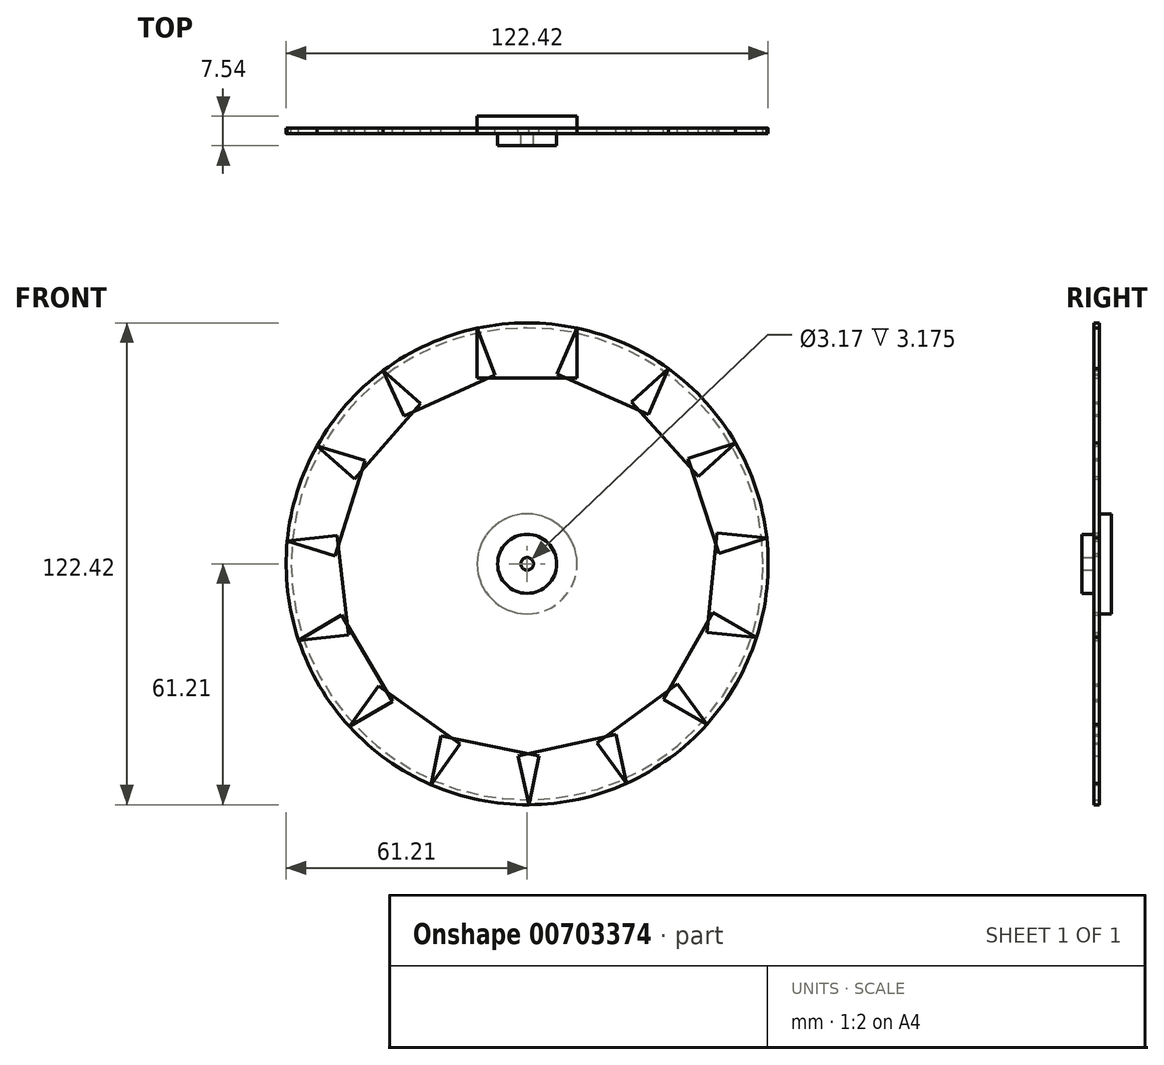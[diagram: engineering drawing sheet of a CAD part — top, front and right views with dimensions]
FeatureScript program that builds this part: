
annotation { "Feature Type Name" : "Feature", "Feature Type Description" : "" }
export const myFeature = defineFeature(function(context is Context, id is Id, definition is map)
    precondition{}
    {
        {
            var Q0;
            Q0=qCreatedBy(makeId("Front.planeOp"),FACE);
            var sketch = newSketch(context, id + "F0", { "sketchPlane" : qUnion([Q0])});
            skCircle(sketch, "E0", {"center": v(0, 0) * mm, "radius": 59.94 * mm});
            skCircle(sketch, "E1", {"center": v(0, 0) * mm, "radius": 61.21 * mm});
            skLineSegment(sketch, "E2.top", {"start": v(-12.7, 47.18) * mm, "end": v(12.7, 47.18) * mm});
            skLineSegment(sketch, "E2.left", {"start": v(-12.7, 59.88) * mm, "end": v(-12.7, 47.18) * mm});
            skLineSegment(sketch, "E2.right", {"start": v(12.7, 59.88) * mm, "end": v(12.7, 47.18) * mm});
            skArc(sketch, "E3", {"start": v(-12.7, 59.88) * mm, "mid": v(0, 61.21) * mm, "end": v(12.7, 59.88) * mm});
            skLineSegment(sketch, "E4.top", {"start": v(7.54, 48.28) * mm, "end": v(30.76, 37.97) * mm});
            skLineSegment(sketch, "E4.left", {"start": v(12.7, 59.88) * mm, "end": v(7.54, 48.28) * mm});
            skLineSegment(sketch, "E4.right", {"start": v(35.91, 49.57) * mm, "end": v(30.76, 37.97) * mm});
            skArc(sketch, "E5", {"start": v(12.7, 59.88) * mm, "mid": v(24.85, 55.94) * mm, "end": v(35.91, 49.57) * mm});
            skLineSegment(sketch, "E6.top", {"start": v(26.5, 41.06) * mm, "end": v(43.52, 22.21) * mm});
            skLineSegment(sketch, "E6.left", {"start": v(35.91, 49.57) * mm, "end": v(26.5, 41.06) * mm});
            skLineSegment(sketch, "E6.right", {"start": v(52.94, 30.73) * mm, "end": v(43.52, 22.21) * mm});
            skArc(sketch, "E7", {"start": v(35.91, 49.57) * mm, "mid": v(45.42, 41.04) * mm, "end": v(52.94, 30.73) * mm});
            skLineSegment(sketch, "E8.top", {"start": v(40.88, 26.77) * mm, "end": v(48.8, 2.63) * mm});
            skLineSegment(sketch, "E8.left", {"start": v(52.94, 30.73) * mm, "end": v(40.88, 26.77) * mm});
            skLineSegment(sketch, "E8.right", {"start": v(60.86, 6.6) * mm, "end": v(48.8, 2.63) * mm});
            skArc(sketch, "E9", {"start": v(52.94, 30.73) * mm, "mid": v(58.17, 19.07) * mm, "end": v(60.86, 6.6) * mm});
            skLineSegment(sketch, "E10.top", {"start": v(48.22, 7.87) * mm, "end": v(45.66, -17.4) * mm});
            skLineSegment(sketch, "E10.left", {"start": v(60.86, 6.6) * mm, "end": v(48.22, 7.87) * mm});
            skLineSegment(sketch, "E10.right", {"start": v(58.3, -18.68) * mm, "end": v(45.66, -17.4) * mm});
            skArc(sketch, "E11", {"start": v(60.86, 6.6) * mm, "mid": v(60.9, -6.18) * mm, "end": v(58.3, -18.68) * mm});
            skLineSegment(sketch, "E12.top", {"start": v(47.27, -12.38) * mm, "end": v(34.67, -34.43) * mm});
            skLineSegment(sketch, "E12.left", {"start": v(58.3, -18.68) * mm, "end": v(47.27, -12.38) * mm});
            skLineSegment(sketch, "E12.right", {"start": v(45.7, -40.73) * mm, "end": v(34.67, -34.43) * mm});
            skArc(sketch, "E13", {"start": v(58.3, -18.68) * mm, "mid": v(53.15, -30.37) * mm, "end": v(45.7, -40.73) * mm});
            skLineSegment(sketch, "E14.top", {"start": v(38.17, -30.5) * mm, "end": v(17.7, -45.54) * mm});
            skLineSegment(sketch, "E14.left", {"start": v(45.7, -40.73) * mm, "end": v(38.17, -30.5) * mm});
            skLineSegment(sketch, "E14.right", {"start": v(25.23, -55.77) * mm, "end": v(17.7, -45.54) * mm});
            skArc(sketch, "E15", {"start": v(45.7, -40.73) * mm, "mid": v(36.25, -49.33) * mm, "end": v(25.23, -55.77) * mm});
            skLineSegment(sketch, "E16.top", {"start": v(22.5, -43.37) * mm, "end": v(-2.3, -48.8) * mm});
            skLineSegment(sketch, "E16.left", {"start": v(25.23, -55.77) * mm, "end": v(22.5, -43.37) * mm});
            skLineSegment(sketch, "E16.right", {"start": v(0.42, -61.21) * mm, "end": v(-2.3, -48.8) * mm});
            skArc(sketch, "E17", {"start": v(25.23, -55.77) * mm, "mid": v(13.1, -59.8) * mm, "end": v(0.42, -61.21) * mm});
            skLineSegment(sketch, "E18.top", {"start": v(2.97, -48.77) * mm, "end": v(-21.92, -43.67) * mm});
            skLineSegment(sketch, "E18.left", {"start": v(0.42, -61.21) * mm, "end": v(2.97, -48.77) * mm});
            skLineSegment(sketch, "E18.right", {"start": v(-24.47, -56.11) * mm, "end": v(-21.92, -43.67) * mm});
            skArc(sketch, "E19", {"start": v(0.42, -61.21) * mm, "mid": v(-12.3, -59.97) * mm, "end": v(-24.47, -56.11) * mm});
            skLineSegment(sketch, "E20.top", {"start": v(-17.09, -45.78) * mm, "end": v(-37.76, -31.01) * mm});
            skLineSegment(sketch, "E20.left", {"start": v(-24.47, -56.11) * mm, "end": v(-17.09, -45.78) * mm});
            skLineSegment(sketch, "E20.right", {"start": v(-45.14, -41.35) * mm, "end": v(-37.76, -31.01) * mm});
            skArc(sketch, "E21", {"start": v(-24.47, -56.11) * mm, "mid": v(-35.58, -49.81) * mm, "end": v(-45.14, -41.35) * mm});
            skLineSegment(sketch, "E22.top", {"start": v(-34.2, -34.9) * mm, "end": v(-47.1, -13.02) * mm});
            skLineSegment(sketch, "E22.left", {"start": v(-45.14, -41.35) * mm, "end": v(-34.2, -34.9) * mm});
            skLineSegment(sketch, "E22.right", {"start": v(-58.04, -19.47) * mm, "end": v(-47.1, -13.02) * mm});
            skArc(sketch, "E23", {"start": v(-45.14, -41.35) * mm, "mid": v(-52.73, -31.09) * mm, "end": v(-58.04, -19.47) * mm});
            skLineSegment(sketch, "E24.top", {"start": v(-45.42, -18.02) * mm, "end": v(-48.33, 7.22) * mm});
            skLineSegment(sketch, "E24.left", {"start": v(-58.04, -19.47) * mm, "end": v(-45.42, -18.02) * mm});
            skLineSegment(sketch, "E24.right", {"start": v(-60.94, 5.76) * mm, "end": v(-48.33, 7.22) * mm});
            skArc(sketch, "E25", {"start": v(-58.04, -19.47) * mm, "mid": v(-60.81, -7) * mm, "end": v(-60.94, 5.76) * mm});
            skLineSegment(sketch, "E26.top", {"start": v(-48.82, 1.97) * mm, "end": v(-41.24, 26.21) * mm});
            skLineSegment(sketch, "E26.left", {"start": v(-60.94, 5.76) * mm, "end": v(-48.82, 1.97) * mm});
            skLineSegment(sketch, "E26.right", {"start": v(-53.36, 30) * mm, "end": v(-41.24, 26.21) * mm});
            skArc(sketch, "E27", {"start": v(-60.94, 5.76) * mm, "mid": v(-58.42, 18.28) * mm, "end": v(-53.36, 30) * mm});
            skLineSegment(sketch, "E28.top", {"start": v(-43.82, 21.62) * mm, "end": v(-27.05, 40.7) * mm});
            skLineSegment(sketch, "E28.left", {"start": v(-53.36, 30) * mm, "end": v(-43.82, 21.62) * mm});
            skLineSegment(sketch, "E28.right", {"start": v(-36.58, 49.08) * mm, "end": v(-27.05, 40.7) * mm});
            skArc(sketch, "E29", {"start": v(-53.36, 30) * mm, "mid": v(-45.97, 40.42) * mm, "end": v(-36.58, 49.08) * mm});
            skLineSegment(sketch, "E30.top", {"start": v(-31.34, 37.51) * mm, "end": v(-8.2, 48) * mm});
            skLineSegment(sketch, "E30.left", {"start": v(-36.58, 49.08) * mm, "end": v(-31.34, 37.51) * mm});
            skArc(sketch, "E31", {"start": v(-36.58, 49.08) * mm, "mid": v(49.94, -35.4) * mm, "end": v(-58.42, 18.28) * mm});
            skArc(sketch, "E32", {"start": v(-58.42, 18.28) * mm, "mid": v(-6.8, 60.84) * mm, "end": v(52.94, 30.73) * mm});
            skCircle(sketch, "E33", {"center": v(0, 0) * mm, "radius": 7.5 * mm});
            skArc(sketch, "E34", {"start": v(-58.42, 18.28) * mm, "mid": v(-41.2, 45.28) * mm, "end": v(-12.7, 59.88) * mm});
            skLineSegment(sketch, "E35", {"start": v(-12.7, 59.88) * mm, "end": v(-8.2, 48) * mm});
            skPoint(sketch, "E36", {"position": v(-35.43, 31.16) * mm});
            skPoint(sketch, "E37", {"position": v(-19.77, 42.76) * mm});
            skPoint(sketch, "E38", {"position": v(0, 47.18) * mm});
            skPoint(sketch, "E39", {"position": v(19.15, 43.12) * mm});
            skPoint(sketch, "E40", {"position": v(35, 31.63) * mm});
            skPoint(sketch, "E41", {"position": v(44.83, 14.7) * mm});
            skPoint(sketch, "E42", {"position": v(46.94, -4.76) * mm});
            skPoint(sketch, "E43", {"position": v(40.97, -23.4) * mm});
            skPoint(sketch, "E44", {"position": v(27.94, -38.02) * mm});
            skPoint(sketch, "E45", {"position": v(10.1, -46.09) * mm});
            skPoint(sketch, "E46", {"position": v(-9.48, -46.22) * mm});
            skPoint(sketch, "E47", {"position": v(-27.42, -38.4) * mm});
            skPoint(sketch, "E48", {"position": v(-40.65, -23.96) * mm});
            skPoint(sketch, "E49", {"position": v(-46.87, -5.4) * mm});
            skPoint(sketch, "E50", {"position": v(-45.03, 14.1) * mm});
            skSolve(sketch);
        }
        {
            var Q0;
            {var subQ7=sQuery(id+"F0.wireOp",EDGE,"E0");var subQ9=sQuery(id+"F0.wireOp",EDGE,"E6.left");var subQ10=makeQuery(id+"F0.imprint","INTERSECT",VERTEX,{"derivedFrom":[subQ7,subQ9]});Q0=makeQuery(id+"F0.imprint","IMPRINT",FACE,{"disambiguationData":[TD([[makeQuery(id+"F0.imprint","IMPRINT",EDGE,{"disambiguationData":[TD([[subQ10,-1.0]])],"derivedFrom":subQ7}),1.0]])]});}
            var Q1;
            {var subQ7=sQuery(id+"F0.wireOp",EDGE,"E0");var subQ9=sQuery(id+"F0.wireOp",EDGE,"E20.left");var subQ10=makeQuery(id+"F0.imprint","INTERSECT",VERTEX,{"derivedFrom":[subQ7,subQ9]});Q1=makeQuery(id+"F0.imprint","IMPRINT",FACE,{"disambiguationData":[TD([[makeQuery(id+"F0.imprint","IMPRINT",EDGE,{"disambiguationData":[TD([[subQ10,-1.0]])],"derivedFrom":subQ7}),1.0]])]});}
            var Q2;
            {var subQ0=sQuery(id+"F0.wireOp",EDGE,"E20.right");var subQ3=sQuery(id+"F0.wireOp",EDGE,"E0");var subQ4=makeQuery(id+"F0.imprint","INTERSECT",VERTEX,{"derivedFrom":[subQ3,subQ0]});Q2=makeQuery(id+"F0.imprint","IMPRINT",FACE,{"disambiguationData":[TD([[makeQuery(id+"F0.imprint","IMPRINT",EDGE,{"disambiguationData":[TD([[subQ4,-1.0]])],"derivedFrom":subQ3}),1.0]])]});}
            var Q3;
            {var subQ0=sQuery(id+"F0.wireOp",EDGE,"E14.right");var subQ3=sQuery(id+"F0.wireOp",EDGE,"E0");var subQ4=makeQuery(id+"F0.imprint","INTERSECT",VERTEX,{"derivedFrom":[subQ3,subQ0]});Q3=makeQuery(id+"F0.imprint","IMPRINT",FACE,{"disambiguationData":[TD([[makeQuery(id+"F0.imprint","IMPRINT",EDGE,{"disambiguationData":[TD([[subQ4,-1.0]])],"derivedFrom":subQ3}),1.0]])]});}
            var Q4;
            {var subQ0=sQuery(id+"F0.wireOp",EDGE,"E10.right");var subQ3=sQuery(id+"F0.wireOp",EDGE,"E0");var subQ4=makeQuery(id+"F0.imprint","INTERSECT",VERTEX,{"derivedFrom":[subQ3,subQ0]});Q4=makeQuery(id+"F0.imprint","IMPRINT",FACE,{"disambiguationData":[TD([[makeQuery(id+"F0.imprint","IMPRINT",EDGE,{"disambiguationData":[TD([[subQ4,-1.0]])],"derivedFrom":subQ3}),1.0]])]});}
            var Q5;
            {var subQ7=sQuery(id+"F0.wireOp",EDGE,"E0");var subQ9=sQuery(id+"F0.wireOp",EDGE,"E26.left");var subQ10=makeQuery(id+"F0.imprint","INTERSECT",VERTEX,{"derivedFrom":[subQ7,subQ9]});Q5=makeQuery(id+"F0.imprint","IMPRINT",FACE,{"disambiguationData":[TD([[makeQuery(id+"F0.imprint","IMPRINT",EDGE,{"disambiguationData":[TD([[subQ10,-1.0]])],"derivedFrom":subQ7}),1.0]])]});}
            var Q6;
            {var subQ5=sQuery(id+"F0.wireOp",EDGE,"E12.right");var subQ7=sQuery(id+"F0.wireOp",EDGE,"E0");var subQ8=makeQuery(id+"F0.imprint","INTERSECT",VERTEX,{"derivedFrom":[subQ7,subQ5]});Q6=makeQuery(id+"F0.imprint","IMPRINT",FACE,{"disambiguationData":[TD([[makeQuery(id+"F0.imprint","IMPRINT",EDGE,{"disambiguationData":[TD([[subQ8,-1.0]])],"derivedFrom":subQ7}),1.0]])]});}
            var Q7;
            {var subQ0=sQuery(id+"F0.wireOp",EDGE,"E26.right");var subQ3=sQuery(id+"F0.wireOp",EDGE,"E0");var subQ4=makeQuery(id+"F0.imprint","INTERSECT",VERTEX,{"derivedFrom":[subQ3,subQ0]});Q7=makeQuery(id+"F0.imprint","IMPRINT",FACE,{"disambiguationData":[TD([[makeQuery(id+"F0.imprint","IMPRINT",EDGE,{"disambiguationData":[TD([[subQ4,-1.0]])],"derivedFrom":subQ3}),1.0]])]});}
            var Q8;
            {var subQ0=sQuery(id+"F0.wireOp",EDGE,"E24.right");var subQ3=sQuery(id+"F0.wireOp",EDGE,"E0");var subQ4=makeQuery(id+"F0.imprint","INTERSECT",VERTEX,{"derivedFrom":[subQ3,subQ0]});Q8=makeQuery(id+"F0.imprint","IMPRINT",FACE,{"disambiguationData":[TD([[makeQuery(id+"F0.imprint","IMPRINT",EDGE,{"disambiguationData":[TD([[subQ4,-1.0]])],"derivedFrom":subQ3}),1.0]])]});}
            var Q9;
            {var subQ5=sQuery(id+"F0.wireOp",EDGE,"E22.right");var subQ7=sQuery(id+"F0.wireOp",EDGE,"E0");var subQ8=makeQuery(id+"F0.imprint","INTERSECT",VERTEX,{"derivedFrom":[subQ7,subQ5]});Q9=makeQuery(id+"F0.imprint","IMPRINT",FACE,{"disambiguationData":[TD([[makeQuery(id+"F0.imprint","IMPRINT",EDGE,{"disambiguationData":[TD([[subQ8,-1.0]])],"derivedFrom":subQ7}),1.0]])]});}
            var Q10;
            {var subQ7=sQuery(id+"F0.wireOp",EDGE,"E0");var subQ9=sQuery(id+"F0.wireOp",EDGE,"E8.left");var subQ10=makeQuery(id+"F0.imprint","INTERSECT",VERTEX,{"derivedFrom":[subQ7,subQ9]});Q10=makeQuery(id+"F0.imprint","IMPRINT",FACE,{"disambiguationData":[TD([[makeQuery(id+"F0.imprint","IMPRINT",EDGE,{"disambiguationData":[TD([[subQ10,-1.0]])],"derivedFrom":subQ7}),1.0]])]});}
            var Q11;
            {var subQ0=sQuery(id+"F0.wireOp",EDGE,"E18.right");var subQ3=sQuery(id+"F0.wireOp",EDGE,"E0");var subQ4=makeQuery(id+"F0.imprint","INTERSECT",VERTEX,{"derivedFrom":[subQ3,subQ0]});Q11=makeQuery(id+"F0.imprint","IMPRINT",FACE,{"disambiguationData":[TD([[makeQuery(id+"F0.imprint","IMPRINT",EDGE,{"disambiguationData":[TD([[subQ4,-1.0]])],"derivedFrom":subQ3}),1.0]])]});}
            var Q12;
            {var subQ7=sQuery(id+"F0.wireOp",EDGE,"E0");var subQ9=sQuery(id+"F0.wireOp",EDGE,"E14.left");var subQ10=makeQuery(id+"F0.imprint","INTERSECT",VERTEX,{"derivedFrom":[subQ7,subQ9]});Q12=makeQuery(id+"F0.imprint","IMPRINT",FACE,{"disambiguationData":[TD([[makeQuery(id+"F0.imprint","IMPRINT",EDGE,{"disambiguationData":[TD([[subQ10,-1.0]])],"derivedFrom":subQ7}),1.0]])]});}
            var Q13;
            {var subQ5=sQuery(id+"F0.wireOp",EDGE,"E2.right");var subQ7=sQuery(id+"F0.wireOp",EDGE,"E0");var subQ8=makeQuery(id+"F0.imprint","INTERSECT",VERTEX,{"derivedFrom":[subQ7,subQ5]});Q13=makeQuery(id+"F0.imprint","IMPRINT",FACE,{"disambiguationData":[TD([[makeQuery(id+"F0.imprint","IMPRINT",EDGE,{"disambiguationData":[TD([[subQ8,-1.0]])],"derivedFrom":subQ7}),1.0]])]});}
            var Q14;
            {var subQ0=sQuery(id+"F0.wireOp",EDGE,"E4.right");var subQ3=sQuery(id+"F0.wireOp",EDGE,"E0");var subQ4=makeQuery(id+"F0.imprint","INTERSECT",VERTEX,{"derivedFrom":[subQ3,subQ0]});Q14=makeQuery(id+"F0.imprint","IMPRINT",FACE,{"disambiguationData":[TD([[makeQuery(id+"F0.imprint","IMPRINT",EDGE,{"disambiguationData":[TD([[subQ4,-1.0]])],"derivedFrom":subQ3}),1.0]])]});}
            var Q15;
            {var subQ0=sQuery(id+"F0.wireOp",EDGE,"E28.right");var subQ3=sQuery(id+"F0.wireOp",EDGE,"E0");var subQ4=makeQuery(id+"F0.imprint","INTERSECT",VERTEX,{"derivedFrom":[subQ3,subQ0]});Q15=makeQuery(id+"F0.imprint","IMPRINT",FACE,{"disambiguationData":[TD([[makeQuery(id+"F0.imprint","IMPRINT",EDGE,{"disambiguationData":[TD([[subQ4,-1.0]])],"derivedFrom":subQ3}),1.0]])]});}
            var Q16;
            {var subQ5=sQuery(id+"F0.wireOp",EDGE,"E24.left");var subQ6=sQuery(id+"F0.wireOp",EDGE,"E0");var subQ7=makeQuery(id+"F0.imprint","INTERSECT",VERTEX,{"derivedFrom":[subQ6,subQ5]});Q16=makeQuery(id+"F0.imprint","IMPRINT",FACE,{"disambiguationData":[TD([[makeQuery(id+"F0.imprint","IMPRINT",EDGE,{"disambiguationData":[TD([[subQ7,-1.0]])],"derivedFrom":subQ6}),1.0]])]});}
            var Q17;
            {var subQ7=sQuery(id+"F0.wireOp",EDGE,"E0");var subQ9=sQuery(id+"F0.wireOp",EDGE,"E28.left");var subQ10=makeQuery(id+"F0.imprint","INTERSECT",VERTEX,{"derivedFrom":[subQ7,subQ9]});Q17=makeQuery(id+"F0.imprint","IMPRINT",FACE,{"disambiguationData":[TD([[makeQuery(id+"F0.imprint","IMPRINT",EDGE,{"disambiguationData":[TD([[subQ10,-1.0]])],"derivedFrom":subQ7}),1.0]])]});}
            var Q18;
            {var subQ3=sQuery(id+"F0.wireOp",EDGE,"E0");var subQ5=sQuery(id+"F0.wireOp",EDGE,"E22.left");var subQ6=makeQuery(id+"F0.imprint","INTERSECT",VERTEX,{"derivedFrom":[subQ3,subQ5]});Q18=makeQuery(id+"F0.imprint","IMPRINT",FACE,{"disambiguationData":[TD([[makeQuery(id+"F0.imprint","IMPRINT",EDGE,{"disambiguationData":[TD([[subQ6,-1.0]])],"derivedFrom":subQ3}),1.0]])]});}
            var Q19;
            {var subQ0=sQuery(id+"F0.wireOp",EDGE,"E16.right");var subQ3=sQuery(id+"F0.wireOp",EDGE,"E0");var subQ4=makeQuery(id+"F0.imprint","INTERSECT",VERTEX,{"derivedFrom":[subQ3,subQ0]});Q19=makeQuery(id+"F0.imprint","IMPRINT",FACE,{"disambiguationData":[TD([[makeQuery(id+"F0.imprint","IMPRINT",EDGE,{"disambiguationData":[TD([[subQ4,-1.0]])],"derivedFrom":subQ3}),1.0]])]});}
            var Q20;
            {var subQ0=sQuery(id+"F0.wireOp",EDGE,"E8.right");var subQ3=sQuery(id+"F0.wireOp",EDGE,"E0");var subQ4=makeQuery(id+"F0.imprint","INTERSECT",VERTEX,{"derivedFrom":[subQ3,subQ0]});Q20=makeQuery(id+"F0.imprint","IMPRINT",FACE,{"disambiguationData":[TD([[makeQuery(id+"F0.imprint","IMPRINT",EDGE,{"disambiguationData":[TD([[subQ4,1.0]])],"derivedFrom":subQ3}),1.0]])]});}
            var Q21;
            Q21=makeQuery(id+"F0.imprint","IMPRINT",FACE,{"disambiguationData":[TD([[makeQuery(id+"F0.imprint","IMPRINT",EDGE,{"derivedFrom":sQuery(id+"F0.wireOp",EDGE,"E33")}),-1.0]])]});
            var Q22;
            {var subQ7=sQuery(id+"F0.wireOp",EDGE,"E0");var subQ9=sQuery(id+"F0.wireOp",EDGE,"E16.left");var subQ10=makeQuery(id+"F0.imprint","INTERSECT",VERTEX,{"derivedFrom":[subQ7,subQ9]});Q22=makeQuery(id+"F0.imprint","IMPRINT",FACE,{"disambiguationData":[TD([[makeQuery(id+"F0.imprint","IMPRINT",EDGE,{"disambiguationData":[TD([[subQ10,-1.0]])],"derivedFrom":subQ7}),1.0]])]});}
            var Q23;
            {var subQ5=sQuery(id+"F0.wireOp",EDGE,"E10.left");var subQ6=sQuery(id+"F0.wireOp",EDGE,"E0");var subQ7=makeQuery(id+"F0.imprint","INTERSECT",VERTEX,{"derivedFrom":[subQ6,subQ5]});Q23=makeQuery(id+"F0.imprint","IMPRINT",FACE,{"disambiguationData":[TD([[makeQuery(id+"F0.imprint","IMPRINT",EDGE,{"disambiguationData":[TD([[subQ7,-1.0]])],"derivedFrom":subQ6}),1.0]])]});}
            var Q24;
            {var subQ3=sQuery(id+"F0.wireOp",EDGE,"E0");var subQ5=sQuery(id+"F0.wireOp",EDGE,"E10.left");var subQ9=makeQuery(id+"F0.imprint","INTERSECT",VERTEX,{"derivedFrom":[subQ3,subQ5]});Q24=makeQuery(id+"F0.imprint","IMPRINT",FACE,{"disambiguationData":[TD([[makeQuery(id+"F0.imprint","IMPRINT",EDGE,{"disambiguationData":[TD([[subQ9,1.0]])],"derivedFrom":subQ3}),1.0]])]});}
            var Q25;
            {var subQ0=sQuery(id+"F0.wireOp",EDGE,"E6.right");var subQ3=sQuery(id+"F0.wireOp",EDGE,"E0");var subQ4=makeQuery(id+"F0.imprint","INTERSECT",VERTEX,{"derivedFrom":[subQ3,subQ0]});Q25=makeQuery(id+"F0.imprint","IMPRINT",FACE,{"disambiguationData":[TD([[makeQuery(id+"F0.imprint","IMPRINT",EDGE,{"disambiguationData":[TD([[subQ4,-1.0]])],"derivedFrom":subQ3}),1.0]])]});}
            var Q26;
            {var subQ3=sQuery(id+"F0.wireOp",EDGE,"E0");var subQ5=sQuery(id+"F0.wireOp",EDGE,"E35");var subQ9=makeQuery(id+"F0.imprint","INTERSECT",VERTEX,{"derivedFrom":[subQ3,subQ5]});Q26=makeQuery(id+"F0.imprint","IMPRINT",FACE,{"disambiguationData":[TD([[makeQuery(id+"F0.imprint","IMPRINT",EDGE,{"disambiguationData":[TD([[subQ9,-1.0]])],"derivedFrom":subQ3}),1.0]])]});}
            var Q27;
            {var subQ7=sQuery(id+"F0.wireOp",EDGE,"E18.left");var subQ8=sQuery(id+"F0.wireOp",EDGE,"E0");var subQ9=makeQuery(id+"F0.imprint","INTERSECT",VERTEX,{"derivedFrom":[subQ8,subQ7]});Q27=makeQuery(id+"F0.imprint","IMPRINT",FACE,{"disambiguationData":[TD([[makeQuery(id+"F0.imprint","IMPRINT",EDGE,{"disambiguationData":[TD([[subQ9,-1.0]])],"derivedFrom":subQ8}),1.0]])]});}
            var Q28;
            {var subQ7=sQuery(id+"F0.wireOp",EDGE,"E0");var subQ9=sQuery(id+"F0.wireOp",EDGE,"E30.left");var subQ10=makeQuery(id+"F0.imprint","INTERSECT",VERTEX,{"derivedFrom":[subQ7,subQ9]});Q28=makeQuery(id+"F0.imprint","IMPRINT",FACE,{"disambiguationData":[TD([[makeQuery(id+"F0.imprint","IMPRINT",EDGE,{"disambiguationData":[TD([[subQ10,-1.0]])],"derivedFrom":subQ7}),1.0]])]});}
            var Q29;
            {var subQ5=sQuery(id+"F0.wireOp",EDGE,"E2.left");var subQ9=sQuery(id+"F0.wireOp",EDGE,"E0");var subQ10=makeQuery(id+"F0.imprint","INTERSECT",VERTEX,{"derivedFrom":[subQ9,subQ5]});Q29=makeQuery(id+"F0.imprint","IMPRINT",FACE,{"disambiguationData":[TD([[makeQuery(id+"F0.imprint","IMPRINT",EDGE,{"disambiguationData":[TD([[subQ10,-1.0]])],"derivedFrom":subQ9}),1.0]])]});}
            var Q30;
            {var subQ0=sQuery(id+"F0.wireOp",EDGE,"E4.left");var subQ3=sQuery(id+"F0.wireOp",EDGE,"E0");var subQ4=makeQuery(id+"F0.imprint","INTERSECT",VERTEX,{"derivedFrom":[subQ3,subQ0]});Q30=makeQuery(id+"F0.imprint","IMPRINT",FACE,{"disambiguationData":[TD([[makeQuery(id+"F0.imprint","IMPRINT",EDGE,{"disambiguationData":[TD([[subQ4,-1.0]])],"derivedFrom":subQ3}),1.0]])]});}
            extrude(context, id + "F1", {"entities" : qUnion([Q0, Q1, Q2, Q3, Q4, Q5, Q6, Q7, Q8, Q9, Q10, Q11, Q12, Q13, Q14, Q15, Q16, Q17, Q18, Q19, Q20, Q21, Q22, Q23, Q24, Q25, Q26, Q27, Q28, Q29, Q30]), "depth" : 1.2 * mm, "offsetDistance" : 25.4 * mm, "symmetric" : true});
        }
        {
            var Q0;
            {var subQ7=sQuery(id+"F0.wireOp",EDGE,"E0");var subQ9=sQuery(id+"F0.wireOp",EDGE,"E8.left");var subQ10=makeQuery(id+"F0.imprint","INTERSECT",VERTEX,{"derivedFrom":[subQ7,subQ9]});Q0=makeQuery(id+"F0.imprint","IMPRINT",FACE,{"disambiguationData":[TD([[makeQuery(id+"F0.imprint","IMPRINT",EDGE,{"disambiguationData":[TD([[subQ10,-1.0]])],"derivedFrom":subQ7}),1.0]])]});}
            var Q1;
            {var subQ0=sQuery(id+"F0.wireOp",EDGE,"E6.right");var subQ3=sQuery(id+"F0.wireOp",EDGE,"E0");var subQ4=makeQuery(id+"F0.imprint","INTERSECT",VERTEX,{"derivedFrom":[subQ3,subQ0]});Q1=makeQuery(id+"F0.imprint","IMPRINT",FACE,{"disambiguationData":[TD([[makeQuery(id+"F0.imprint","IMPRINT",EDGE,{"disambiguationData":[TD([[subQ4,-1.0]])],"derivedFrom":subQ3}),1.0]])]});}
            var Q2;
            {var subQ0=sQuery(id+"F0.wireOp",EDGE,"E4.right");var subQ3=sQuery(id+"F0.wireOp",EDGE,"E0");var subQ4=makeQuery(id+"F0.imprint","INTERSECT",VERTEX,{"derivedFrom":[subQ3,subQ0]});Q2=makeQuery(id+"F0.imprint","IMPRINT",FACE,{"disambiguationData":[TD([[makeQuery(id+"F0.imprint","IMPRINT",EDGE,{"disambiguationData":[TD([[subQ4,-1.0]])],"derivedFrom":subQ3}),1.0]])]});}
            var Q3;
            {var subQ0=sQuery(id+"F0.wireOp",EDGE,"E8.left");var subQ1=sQuery(id+"F0.wireOp",EDGE,"E0");var subQ2=makeQuery(id+"F0.imprint","INTERSECT",VERTEX,{"derivedFrom":[subQ1,subQ0]});Q3=makeQuery(id+"F0.imprint","IMPRINT",FACE,{"disambiguationData":[TD([[makeQuery(id+"F0.imprint","IMPRINT",EDGE,{"disambiguationData":[TD([[subQ2,-1.0]])],"derivedFrom":subQ1}),-1.0]])]});}
            var Q4;
            {var subQ0=sQuery(id+"F0.wireOp",EDGE,"E6.right");var subQ1=sQuery(id+"F0.wireOp",EDGE,"E0");var subQ2=makeQuery(id+"F0.imprint","INTERSECT",VERTEX,{"derivedFrom":[subQ1,subQ0]});Q4=makeQuery(id+"F0.imprint","IMPRINT",FACE,{"disambiguationData":[TD([[makeQuery(id+"F0.imprint","IMPRINT",EDGE,{"disambiguationData":[TD([[subQ2,-1.0]])],"derivedFrom":subQ1}),-1.0]])]});}
            var Q5;
            {var subQ0=sQuery(id+"F0.wireOp",EDGE,"E4.right");var subQ1=sQuery(id+"F0.wireOp",EDGE,"E0");var subQ2=makeQuery(id+"F0.imprint","INTERSECT",VERTEX,{"derivedFrom":[subQ1,subQ0]});Q5=makeQuery(id+"F0.imprint","IMPRINT",FACE,{"disambiguationData":[TD([[makeQuery(id+"F0.imprint","IMPRINT",EDGE,{"disambiguationData":[TD([[subQ2,-1.0]])],"derivedFrom":subQ1}),-1.0]])]});}
            extrude(context, id + "F2", {"entities" : qUnion([Q0, Q1, Q2, Q3, Q4, Q5]), "depth" : 1.2 * mm + .18 * mm, "offsetDistance" : 25.4 * mm, "symmetric" : true});
        }
        {
            var Q0;
            {var subQ0=sQuery(id+"F0.wireOp",EDGE,"E6.right");var subQ3=sQuery(id+"F0.wireOp",EDGE,"E0");var subQ4=makeQuery(id+"F0.imprint","INTERSECT",VERTEX,{"derivedFrom":[subQ3,subQ0]});Q0=makeQuery(id+"F0.imprint","IMPRINT",FACE,{"disambiguationData":[TD([[makeQuery(id+"F0.imprint","IMPRINT",EDGE,{"disambiguationData":[TD([[subQ4,-1.0]])],"derivedFrom":subQ3}),1.0]])]});}
            var Q1;
            {var subQ3=sQuery(id+"F0.wireOp",EDGE,"E0");var subQ9=sQuery(id+"F0.wireOp",EDGE,"E10.left");var subQ10=makeQuery(id+"F0.imprint","INTERSECT",VERTEX,{"derivedFrom":[subQ3,subQ9]});Q1=makeQuery(id+"F0.imprint","IMPRINT",FACE,{"disambiguationData":[TD([[makeQuery(id+"F0.imprint","IMPRINT",EDGE,{"disambiguationData":[TD([[subQ10,-1.0]])],"derivedFrom":subQ3}),1.0]])]});}
            var Q2;
            {var subQ0=sQuery(id+"F0.wireOp",EDGE,"E10.left");var subQ1=sQuery(id+"F0.wireOp",EDGE,"E0");var subQ2=makeQuery(id+"F0.imprint","INTERSECT",VERTEX,{"derivedFrom":[subQ1,subQ0]});Q2=makeQuery(id+"F0.imprint","IMPRINT",FACE,{"disambiguationData":[TD([[makeQuery(id+"F0.imprint","IMPRINT",EDGE,{"disambiguationData":[TD([[subQ2,-1.0]])],"derivedFrom":subQ1}),-1.0]])]});}
            var Q3;
            {var subQ3=sQuery(id+"F0.wireOp",EDGE,"E0");var subQ5=sQuery(id+"F0.wireOp",EDGE,"E10.left");var subQ9=makeQuery(id+"F0.imprint","INTERSECT",VERTEX,{"derivedFrom":[subQ3,subQ5]});Q3=makeQuery(id+"F0.imprint","IMPRINT",FACE,{"disambiguationData":[TD([[makeQuery(id+"F0.imprint","IMPRINT",EDGE,{"disambiguationData":[TD([[subQ9,1.0]])],"derivedFrom":subQ3}),1.0]])]});}
            var Q4;
            {var subQ0=sQuery(id+"F0.wireOp",EDGE,"E10.left");var subQ1=sQuery(id+"F0.wireOp",EDGE,"E0");var subQ2=makeQuery(id+"F0.imprint","INTERSECT",VERTEX,{"derivedFrom":[subQ1,subQ0]});Q4=makeQuery(id+"F0.imprint","IMPRINT",FACE,{"disambiguationData":[TD([[makeQuery(id+"F0.imprint","IMPRINT",EDGE,{"disambiguationData":[TD([[subQ2,1.0]])],"derivedFrom":subQ1}),-1.0]])]});}
            var Q5;
            {var subQ0=sQuery(id+"F0.wireOp",EDGE,"E6.right");var subQ1=sQuery(id+"F0.wireOp",EDGE,"E0");var subQ2=makeQuery(id+"F0.imprint","INTERSECT",VERTEX,{"derivedFrom":[subQ1,subQ0]});Q5=makeQuery(id+"F0.imprint","IMPRINT",FACE,{"disambiguationData":[TD([[makeQuery(id+"F0.imprint","IMPRINT",EDGE,{"disambiguationData":[TD([[subQ2,-1.0]])],"derivedFrom":subQ1}),-1.0]])]});}
            extrude(context, id + "F3", {"entities" : qUnion([Q0, Q1, Q2, Q3, Q4, Q5]), "depth" : 1.2 * mm + .18 * mm, "offsetDistance" : 25.4 * mm, "symmetric" : true});
        }
        {
            var Q0;
            {var subQ0=sQuery(id+"F0.wireOp",EDGE,"E10.right");var subQ1=sQuery(id+"F0.wireOp",EDGE,"E0");var subQ2=makeQuery(id+"F0.imprint","INTERSECT",VERTEX,{"derivedFrom":[subQ1,subQ0]});Q0=makeQuery(id+"F0.imprint","IMPRINT",FACE,{"disambiguationData":[TD([[makeQuery(id+"F0.imprint","IMPRINT",EDGE,{"disambiguationData":[TD([[subQ2,-1.0]])],"derivedFrom":subQ1}),-1.0]])]});}
            var Q1;
            {var subQ0=sQuery(id+"F0.wireOp",EDGE,"E10.right");var subQ3=sQuery(id+"F0.wireOp",EDGE,"E0");var subQ4=makeQuery(id+"F0.imprint","INTERSECT",VERTEX,{"derivedFrom":[subQ3,subQ0]});Q1=makeQuery(id+"F0.imprint","IMPRINT",FACE,{"disambiguationData":[TD([[makeQuery(id+"F0.imprint","IMPRINT",EDGE,{"disambiguationData":[TD([[subQ4,-1.0]])],"derivedFrom":subQ3}),1.0]])]});}
            var Q2;
            {var subQ3=sQuery(id+"F0.wireOp",EDGE,"E0");var subQ5=sQuery(id+"F0.wireOp",EDGE,"E10.left");var subQ9=makeQuery(id+"F0.imprint","INTERSECT",VERTEX,{"derivedFrom":[subQ3,subQ5]});Q2=makeQuery(id+"F0.imprint","IMPRINT",FACE,{"disambiguationData":[TD([[makeQuery(id+"F0.imprint","IMPRINT",EDGE,{"disambiguationData":[TD([[subQ9,1.0]])],"derivedFrom":subQ3}),1.0]])]});}
            var Q3;
            {var subQ5=sQuery(id+"F0.wireOp",EDGE,"E8.right");var subQ7=sQuery(id+"F0.wireOp",EDGE,"E0");var subQ8=makeQuery(id+"F0.imprint","INTERSECT",VERTEX,{"derivedFrom":[subQ7,subQ5]});Q3=makeQuery(id+"F0.imprint","IMPRINT",FACE,{"disambiguationData":[TD([[makeQuery(id+"F0.imprint","IMPRINT",EDGE,{"disambiguationData":[TD([[subQ8,1.0]])],"derivedFrom":subQ7}),1.0]])]});}
            var Q4;
            {var subQ0=sQuery(id+"F0.wireOp",EDGE,"E10.left");var subQ1=sQuery(id+"F0.wireOp",EDGE,"E0");var subQ2=makeQuery(id+"F0.imprint","INTERSECT",VERTEX,{"derivedFrom":[subQ1,subQ0]});Q4=makeQuery(id+"F0.imprint","IMPRINT",FACE,{"disambiguationData":[TD([[makeQuery(id+"F0.imprint","IMPRINT",EDGE,{"disambiguationData":[TD([[subQ2,1.0]])],"derivedFrom":subQ1}),-1.0]])]});}
            var Q5;
            {var subQ0=sQuery(id+"F0.wireOp",EDGE,"E8.right");var subQ1=sQuery(id+"F0.wireOp",EDGE,"E0");var subQ2=makeQuery(id+"F0.imprint","INTERSECT",VERTEX,{"derivedFrom":[subQ1,subQ0]});Q5=makeQuery(id+"F0.imprint","IMPRINT",FACE,{"disambiguationData":[TD([[makeQuery(id+"F0.imprint","IMPRINT",EDGE,{"disambiguationData":[TD([[subQ2,1.0]])],"derivedFrom":subQ1}),-1.0]])]});}
            extrude(context, id + "F4", {"entities" : qUnion([Q0, Q1, Q2, Q3, Q4, Q5]), "depth" : 1.2 * mm + .18 * mm, "offsetDistance" : 25.4 * mm, "symmetric" : true});
        }
        {
            var Q0;
            {var subQ7=sQuery(id+"F0.wireOp",EDGE,"E0");var subQ9=sQuery(id+"F0.wireOp",EDGE,"E14.left");var subQ10=makeQuery(id+"F0.imprint","INTERSECT",VERTEX,{"derivedFrom":[subQ7,subQ9]});Q0=makeQuery(id+"F0.imprint","IMPRINT",FACE,{"disambiguationData":[TD([[makeQuery(id+"F0.imprint","IMPRINT",EDGE,{"disambiguationData":[TD([[subQ10,-1.0]])],"derivedFrom":subQ7}),1.0]])]});}
            var Q1;
            {var subQ0=sQuery(id+"F0.wireOp",EDGE,"E10.right");var subQ3=sQuery(id+"F0.wireOp",EDGE,"E0");var subQ4=makeQuery(id+"F0.imprint","INTERSECT",VERTEX,{"derivedFrom":[subQ3,subQ0]});Q1=makeQuery(id+"F0.imprint","IMPRINT",FACE,{"disambiguationData":[TD([[makeQuery(id+"F0.imprint","IMPRINT",EDGE,{"disambiguationData":[TD([[subQ4,-1.0]])],"derivedFrom":subQ3}),1.0]])]});}
            var Q2;
            {var subQ0=sQuery(id+"F0.wireOp",EDGE,"E14.left");var subQ1=sQuery(id+"F0.wireOp",EDGE,"E0");var subQ2=makeQuery(id+"F0.imprint","INTERSECT",VERTEX,{"derivedFrom":[subQ1,subQ0]});Q2=makeQuery(id+"F0.imprint","IMPRINT",FACE,{"disambiguationData":[TD([[makeQuery(id+"F0.imprint","IMPRINT",EDGE,{"disambiguationData":[TD([[subQ2,-1.0]])],"derivedFrom":subQ1}),-1.0]])]});}
            var Q3;
            {var subQ0=sQuery(id+"F0.wireOp",EDGE,"E12.right");var subQ3=sQuery(id+"F0.wireOp",EDGE,"E0");var subQ4=makeQuery(id+"F0.imprint","INTERSECT",VERTEX,{"derivedFrom":[subQ3,subQ0]});Q3=makeQuery(id+"F0.imprint","IMPRINT",FACE,{"disambiguationData":[TD([[makeQuery(id+"F0.imprint","IMPRINT",EDGE,{"disambiguationData":[TD([[subQ4,-1.0]])],"derivedFrom":subQ3}),1.0]])]});}
            var Q4;
            {var subQ0=sQuery(id+"F0.wireOp",EDGE,"E10.right");var subQ1=sQuery(id+"F0.wireOp",EDGE,"E0");var subQ2=makeQuery(id+"F0.imprint","INTERSECT",VERTEX,{"derivedFrom":[subQ1,subQ0]});Q4=makeQuery(id+"F0.imprint","IMPRINT",FACE,{"disambiguationData":[TD([[makeQuery(id+"F0.imprint","IMPRINT",EDGE,{"disambiguationData":[TD([[subQ2,-1.0]])],"derivedFrom":subQ1}),-1.0]])]});}
            var Q5;
            {var subQ0=sQuery(id+"F0.wireOp",EDGE,"E12.right");var subQ1=sQuery(id+"F0.wireOp",EDGE,"E0");var subQ2=makeQuery(id+"F0.imprint","INTERSECT",VERTEX,{"derivedFrom":[subQ1,subQ0]});Q5=makeQuery(id+"F0.imprint","IMPRINT",FACE,{"disambiguationData":[TD([[makeQuery(id+"F0.imprint","IMPRINT",EDGE,{"disambiguationData":[TD([[subQ2,-1.0]])],"derivedFrom":subQ1}),-1.0]])]});}
            extrude(context, id + "F5", {"entities" : qUnion([Q0, Q1, Q2, Q3, Q4, Q5]), "depth" : 1.2 * mm + .18 * mm, "offsetDistance" : 25.4 * mm, "symmetric" : true});
        }
        {
            var Q0;
            {var subQ3=sQuery(id+"F0.wireOp",EDGE,"E0");var subQ9=sQuery(id+"F0.wireOp",EDGE,"E16.left");var subQ10=makeQuery(id+"F0.imprint","INTERSECT",VERTEX,{"derivedFrom":[subQ3,subQ9]});Q0=makeQuery(id+"F0.imprint","IMPRINT",FACE,{"disambiguationData":[TD([[makeQuery(id+"F0.imprint","IMPRINT",EDGE,{"disambiguationData":[TD([[subQ10,-1.0]])],"derivedFrom":subQ3}),1.0]])]});}
            var Q1;
            {var subQ0=sQuery(id+"F0.wireOp",EDGE,"E12.right");var subQ3=sQuery(id+"F0.wireOp",EDGE,"E0");var subQ4=makeQuery(id+"F0.imprint","INTERSECT",VERTEX,{"derivedFrom":[subQ3,subQ0]});Q1=makeQuery(id+"F0.imprint","IMPRINT",FACE,{"disambiguationData":[TD([[makeQuery(id+"F0.imprint","IMPRINT",EDGE,{"disambiguationData":[TD([[subQ4,-1.0]])],"derivedFrom":subQ3}),1.0]])]});}
            var Q2;
            {var subQ0=sQuery(id+"F0.wireOp",EDGE,"E14.right");var subQ3=sQuery(id+"F0.wireOp",EDGE,"E0");var subQ4=makeQuery(id+"F0.imprint","INTERSECT",VERTEX,{"derivedFrom":[subQ3,subQ0]});Q2=makeQuery(id+"F0.imprint","IMPRINT",FACE,{"disambiguationData":[TD([[makeQuery(id+"F0.imprint","IMPRINT",EDGE,{"disambiguationData":[TD([[subQ4,-1.0]])],"derivedFrom":subQ3}),1.0]])]});}
            var Q3;
            {var subQ0=sQuery(id+"F0.wireOp",EDGE,"E16.left");var subQ1=sQuery(id+"F0.wireOp",EDGE,"E0");var subQ2=makeQuery(id+"F0.imprint","INTERSECT",VERTEX,{"derivedFrom":[subQ1,subQ0]});Q3=makeQuery(id+"F0.imprint","IMPRINT",FACE,{"disambiguationData":[TD([[makeQuery(id+"F0.imprint","IMPRINT",EDGE,{"disambiguationData":[TD([[subQ2,-1.0]])],"derivedFrom":subQ1}),-1.0]])]});}
            var Q4;
            {var subQ0=sQuery(id+"F0.wireOp",EDGE,"E12.right");var subQ1=sQuery(id+"F0.wireOp",EDGE,"E0");var subQ2=makeQuery(id+"F0.imprint","INTERSECT",VERTEX,{"derivedFrom":[subQ1,subQ0]});Q4=makeQuery(id+"F0.imprint","IMPRINT",FACE,{"disambiguationData":[TD([[makeQuery(id+"F0.imprint","IMPRINT",EDGE,{"disambiguationData":[TD([[subQ2,-1.0]])],"derivedFrom":subQ1}),-1.0]])]});}
            var Q5;
            {var subQ0=sQuery(id+"F0.wireOp",EDGE,"E14.right");var subQ1=sQuery(id+"F0.wireOp",EDGE,"E0");var subQ2=makeQuery(id+"F0.imprint","INTERSECT",VERTEX,{"derivedFrom":[subQ1,subQ0]});Q5=makeQuery(id+"F0.imprint","IMPRINT",FACE,{"disambiguationData":[TD([[makeQuery(id+"F0.imprint","IMPRINT",EDGE,{"disambiguationData":[TD([[subQ2,-1.0]])],"derivedFrom":subQ1}),-1.0]])]});}
            extrude(context, id + "F6", {"entities" : qUnion([Q0, Q1, Q2, Q3, Q4, Q5]), "depth" : 1.2 * mm + .18 * mm, "offsetDistance" : 25.4 * mm, "symmetric" : true});
        }
        {
            var Q0;
            {var subQ7=sQuery(id+"F0.wireOp",EDGE,"E0");var subQ9=sQuery(id+"F0.wireOp",EDGE,"E18.left");var subQ10=makeQuery(id+"F0.imprint","INTERSECT",VERTEX,{"derivedFrom":[subQ7,subQ9]});Q0=makeQuery(id+"F0.imprint","IMPRINT",FACE,{"disambiguationData":[TD([[makeQuery(id+"F0.imprint","IMPRINT",EDGE,{"disambiguationData":[TD([[subQ10,-1.0]])],"derivedFrom":subQ7}),1.0]])]});}
            var Q1;
            {var subQ5=sQuery(id+"F0.wireOp",EDGE,"E16.right");var subQ7=sQuery(id+"F0.wireOp",EDGE,"E0");var subQ8=makeQuery(id+"F0.imprint","INTERSECT",VERTEX,{"derivedFrom":[subQ7,subQ5]});Q1=makeQuery(id+"F0.imprint","IMPRINT",FACE,{"disambiguationData":[TD([[makeQuery(id+"F0.imprint","IMPRINT",EDGE,{"disambiguationData":[TD([[subQ8,-1.0]])],"derivedFrom":subQ7}),1.0]])]});}
            var Q2;
            {var subQ0=sQuery(id+"F0.wireOp",EDGE,"E18.left");var subQ1=sQuery(id+"F0.wireOp",EDGE,"E0");var subQ2=makeQuery(id+"F0.imprint","INTERSECT",VERTEX,{"derivedFrom":[subQ1,subQ0]});Q2=makeQuery(id+"F0.imprint","IMPRINT",FACE,{"disambiguationData":[TD([[makeQuery(id+"F0.imprint","IMPRINT",EDGE,{"disambiguationData":[TD([[subQ2,-1.0]])],"derivedFrom":subQ1}),-1.0]])]});}
            var Q3;
            {var subQ0=sQuery(id+"F0.wireOp",EDGE,"E14.right");var subQ3=sQuery(id+"F0.wireOp",EDGE,"E0");var subQ4=makeQuery(id+"F0.imprint","INTERSECT",VERTEX,{"derivedFrom":[subQ3,subQ0]});Q3=makeQuery(id+"F0.imprint","IMPRINT",FACE,{"disambiguationData":[TD([[makeQuery(id+"F0.imprint","IMPRINT",EDGE,{"disambiguationData":[TD([[subQ4,-1.0]])],"derivedFrom":subQ3}),1.0]])]});}
            var Q4;
            {var subQ0=sQuery(id+"F0.wireOp",EDGE,"E16.right");var subQ1=sQuery(id+"F0.wireOp",EDGE,"E0");var subQ2=makeQuery(id+"F0.imprint","INTERSECT",VERTEX,{"derivedFrom":[subQ1,subQ0]});Q4=makeQuery(id+"F0.imprint","IMPRINT",FACE,{"disambiguationData":[TD([[makeQuery(id+"F0.imprint","IMPRINT",EDGE,{"disambiguationData":[TD([[subQ2,-1.0]])],"derivedFrom":subQ1}),-1.0]])]});}
            var Q5;
            {var subQ0=sQuery(id+"F0.wireOp",EDGE,"E14.right");var subQ1=sQuery(id+"F0.wireOp",EDGE,"E0");var subQ2=makeQuery(id+"F0.imprint","INTERSECT",VERTEX,{"derivedFrom":[subQ1,subQ0]});Q5=makeQuery(id+"F0.imprint","IMPRINT",FACE,{"disambiguationData":[TD([[makeQuery(id+"F0.imprint","IMPRINT",EDGE,{"disambiguationData":[TD([[subQ2,-1.0]])],"derivedFrom":subQ1}),-1.0]])]});}
            extrude(context, id + "F7", {"entities" : qUnion([Q0, Q1, Q2, Q3, Q4, Q5]), "depth" : 1.2 * mm + .18 * mm, "offsetDistance" : 25.4 * mm, "symmetric" : true});
        }
        {
            var Q0;
            {var subQ7=sQuery(id+"F0.wireOp",EDGE,"E0");var subQ9=sQuery(id+"F0.wireOp",EDGE,"E20.left");var subQ10=makeQuery(id+"F0.imprint","INTERSECT",VERTEX,{"derivedFrom":[subQ7,subQ9]});Q0=makeQuery(id+"F0.imprint","IMPRINT",FACE,{"disambiguationData":[TD([[makeQuery(id+"F0.imprint","IMPRINT",EDGE,{"disambiguationData":[TD([[subQ10,-1.0]])],"derivedFrom":subQ7}),1.0]])]});}
            var Q1;
            {var subQ0=sQuery(id+"F0.wireOp",EDGE,"E18.right");var subQ3=sQuery(id+"F0.wireOp",EDGE,"E0");var subQ4=makeQuery(id+"F0.imprint","INTERSECT",VERTEX,{"derivedFrom":[subQ3,subQ0]});Q1=makeQuery(id+"F0.imprint","IMPRINT",FACE,{"disambiguationData":[TD([[makeQuery(id+"F0.imprint","IMPRINT",EDGE,{"disambiguationData":[TD([[subQ4,-1.0]])],"derivedFrom":subQ3}),1.0]])]});}
            var Q2;
            {var subQ5=sQuery(id+"F0.wireOp",EDGE,"E16.right");var subQ7=sQuery(id+"F0.wireOp",EDGE,"E0");var subQ8=makeQuery(id+"F0.imprint","INTERSECT",VERTEX,{"derivedFrom":[subQ7,subQ5]});Q2=makeQuery(id+"F0.imprint","IMPRINT",FACE,{"disambiguationData":[TD([[makeQuery(id+"F0.imprint","IMPRINT",EDGE,{"disambiguationData":[TD([[subQ8,-1.0]])],"derivedFrom":subQ7}),1.0]])]});}
            var Q3;
            {var subQ0=sQuery(id+"F0.wireOp",EDGE,"E20.left");var subQ1=sQuery(id+"F0.wireOp",EDGE,"E0");var subQ2=makeQuery(id+"F0.imprint","INTERSECT",VERTEX,{"derivedFrom":[subQ1,subQ0]});Q3=makeQuery(id+"F0.imprint","IMPRINT",FACE,{"disambiguationData":[TD([[makeQuery(id+"F0.imprint","IMPRINT",EDGE,{"disambiguationData":[TD([[subQ2,-1.0]])],"derivedFrom":subQ1}),-1.0]])]});}
            var Q4;
            {var subQ0=sQuery(id+"F0.wireOp",EDGE,"E16.right");var subQ1=sQuery(id+"F0.wireOp",EDGE,"E0");var subQ2=makeQuery(id+"F0.imprint","INTERSECT",VERTEX,{"derivedFrom":[subQ1,subQ0]});Q4=makeQuery(id+"F0.imprint","IMPRINT",FACE,{"disambiguationData":[TD([[makeQuery(id+"F0.imprint","IMPRINT",EDGE,{"disambiguationData":[TD([[subQ2,-1.0]])],"derivedFrom":subQ1}),-1.0]])]});}
            var Q5;
            {var subQ0=sQuery(id+"F0.wireOp",EDGE,"E18.right");var subQ1=sQuery(id+"F0.wireOp",EDGE,"E0");var subQ2=makeQuery(id+"F0.imprint","INTERSECT",VERTEX,{"derivedFrom":[subQ1,subQ0]});Q5=makeQuery(id+"F0.imprint","IMPRINT",FACE,{"disambiguationData":[TD([[makeQuery(id+"F0.imprint","IMPRINT",EDGE,{"disambiguationData":[TD([[subQ2,-1.0]])],"derivedFrom":subQ1}),-1.0]])]});}
            extrude(context, id + "F8", {"entities" : qUnion([Q0, Q1, Q2, Q3, Q4, Q5]), "depth" : 1.2 * mm + .18 * mm, "offsetDistance" : 25.4 * mm, "symmetric" : true});
        }
        {
            var Q0;
            {var subQ0=sQuery(id+"F0.wireOp",EDGE,"E18.right");var subQ1=sQuery(id+"F0.wireOp",EDGE,"E0");var subQ2=makeQuery(id+"F0.imprint","INTERSECT",VERTEX,{"derivedFrom":[subQ1,subQ0]});Q0=makeQuery(id+"F0.imprint","IMPRINT",FACE,{"disambiguationData":[TD([[makeQuery(id+"F0.imprint","IMPRINT",EDGE,{"disambiguationData":[TD([[subQ2,-1.0]])],"derivedFrom":subQ1}),-1.0]])]});}
            var Q1;
            {var subQ0=sQuery(id+"F0.wireOp",EDGE,"E22.left");var subQ1=sQuery(id+"F0.wireOp",EDGE,"E0");var subQ2=makeQuery(id+"F0.imprint","INTERSECT",VERTEX,{"derivedFrom":[subQ1,subQ0]});Q1=makeQuery(id+"F0.imprint","IMPRINT",FACE,{"disambiguationData":[TD([[makeQuery(id+"F0.imprint","IMPRINT",EDGE,{"disambiguationData":[TD([[subQ2,-1.0]])],"derivedFrom":subQ1}),-1.0]])]});}
            var Q2;
            {var subQ0=sQuery(id+"F0.wireOp",EDGE,"E18.right");var subQ3=sQuery(id+"F0.wireOp",EDGE,"E0");var subQ4=makeQuery(id+"F0.imprint","INTERSECT",VERTEX,{"derivedFrom":[subQ3,subQ0]});Q2=makeQuery(id+"F0.imprint","IMPRINT",FACE,{"disambiguationData":[TD([[makeQuery(id+"F0.imprint","IMPRINT",EDGE,{"disambiguationData":[TD([[subQ4,-1.0]])],"derivedFrom":subQ3}),1.0]])]});}
            var Q3;
            {var subQ7=sQuery(id+"F0.wireOp",EDGE,"E0");var subQ9=sQuery(id+"F0.wireOp",EDGE,"E22.left");var subQ10=makeQuery(id+"F0.imprint","INTERSECT",VERTEX,{"derivedFrom":[subQ7,subQ9]});Q3=makeQuery(id+"F0.imprint","IMPRINT",FACE,{"disambiguationData":[TD([[makeQuery(id+"F0.imprint","IMPRINT",EDGE,{"disambiguationData":[TD([[subQ10,-1.0]])],"derivedFrom":subQ7}),1.0]])]});}
            var Q4;
            {var subQ0=sQuery(id+"F0.wireOp",EDGE,"E20.right");var subQ3=sQuery(id+"F0.wireOp",EDGE,"E0");var subQ4=makeQuery(id+"F0.imprint","INTERSECT",VERTEX,{"derivedFrom":[subQ3,subQ0]});Q4=makeQuery(id+"F0.imprint","IMPRINT",FACE,{"disambiguationData":[TD([[makeQuery(id+"F0.imprint","IMPRINT",EDGE,{"disambiguationData":[TD([[subQ4,-1.0]])],"derivedFrom":subQ3}),1.0]])]});}
            var Q5;
            {var subQ0=sQuery(id+"F0.wireOp",EDGE,"E20.right");var subQ1=sQuery(id+"F0.wireOp",EDGE,"E0");var subQ2=makeQuery(id+"F0.imprint","INTERSECT",VERTEX,{"derivedFrom":[subQ1,subQ0]});Q5=makeQuery(id+"F0.imprint","IMPRINT",FACE,{"disambiguationData":[TD([[makeQuery(id+"F0.imprint","IMPRINT",EDGE,{"disambiguationData":[TD([[subQ2,-1.0]])],"derivedFrom":subQ1}),-1.0]])]});}
            extrude(context, id + "F9", {"entities" : qUnion([Q0, Q1, Q2, Q3, Q4, Q5]), "depth" : 1.2 * mm + .18 * mm, "offsetDistance" : 25.4 * mm, "symmetric" : true});
        }
        {
            var Q0;
            {var subQ5=sQuery(id+"F0.wireOp",EDGE,"E24.left");var subQ6=sQuery(id+"F0.wireOp",EDGE,"E0");var subQ7=makeQuery(id+"F0.imprint","INTERSECT",VERTEX,{"derivedFrom":[subQ6,subQ5]});Q0=makeQuery(id+"F0.imprint","IMPRINT",FACE,{"disambiguationData":[TD([[makeQuery(id+"F0.imprint","IMPRINT",EDGE,{"disambiguationData":[TD([[subQ7,-1.0]])],"derivedFrom":subQ6}),1.0]])]});}
            var Q1;
            {var subQ5=sQuery(id+"F0.wireOp",EDGE,"E22.right");var subQ7=sQuery(id+"F0.wireOp",EDGE,"E0");var subQ8=makeQuery(id+"F0.imprint","INTERSECT",VERTEX,{"derivedFrom":[subQ7,subQ5]});Q1=makeQuery(id+"F0.imprint","IMPRINT",FACE,{"disambiguationData":[TD([[makeQuery(id+"F0.imprint","IMPRINT",EDGE,{"disambiguationData":[TD([[subQ8,-1.0]])],"derivedFrom":subQ7}),1.0]])]});}
            var Q2;
            {var subQ0=sQuery(id+"F0.wireOp",EDGE,"E20.right");var subQ3=sQuery(id+"F0.wireOp",EDGE,"E0");var subQ4=makeQuery(id+"F0.imprint","INTERSECT",VERTEX,{"derivedFrom":[subQ3,subQ0]});Q2=makeQuery(id+"F0.imprint","IMPRINT",FACE,{"disambiguationData":[TD([[makeQuery(id+"F0.imprint","IMPRINT",EDGE,{"disambiguationData":[TD([[subQ4,-1.0]])],"derivedFrom":subQ3}),1.0]])]});}
            var Q3;
            {var subQ0=sQuery(id+"F0.wireOp",EDGE,"E24.left");var subQ1=sQuery(id+"F0.wireOp",EDGE,"E0");var subQ2=makeQuery(id+"F0.imprint","INTERSECT",VERTEX,{"derivedFrom":[subQ1,subQ0]});Q3=makeQuery(id+"F0.imprint","IMPRINT",FACE,{"disambiguationData":[TD([[makeQuery(id+"F0.imprint","IMPRINT",EDGE,{"disambiguationData":[TD([[subQ2,-1.0]])],"derivedFrom":subQ1}),-1.0]])]});}
            var Q4;
            {var subQ0=sQuery(id+"F0.wireOp",EDGE,"E20.right");var subQ1=sQuery(id+"F0.wireOp",EDGE,"E0");var subQ2=makeQuery(id+"F0.imprint","INTERSECT",VERTEX,{"derivedFrom":[subQ1,subQ0]});Q4=makeQuery(id+"F0.imprint","IMPRINT",FACE,{"disambiguationData":[TD([[makeQuery(id+"F0.imprint","IMPRINT",EDGE,{"disambiguationData":[TD([[subQ2,-1.0]])],"derivedFrom":subQ1}),-1.0]])]});}
            var Q5;
            {var subQ0=sQuery(id+"F0.wireOp",EDGE,"E22.right");var subQ1=sQuery(id+"F0.wireOp",EDGE,"E0");var subQ2=makeQuery(id+"F0.imprint","INTERSECT",VERTEX,{"derivedFrom":[subQ1,subQ0]});Q5=makeQuery(id+"F0.imprint","IMPRINT",FACE,{"disambiguationData":[TD([[makeQuery(id+"F0.imprint","IMPRINT",EDGE,{"disambiguationData":[TD([[subQ2,-1.0]])],"derivedFrom":subQ1}),-1.0]])]});}
            extrude(context, id + "F10", {"entities" : qUnion([Q0, Q1, Q2, Q3, Q4, Q5]), "depth" : 1.2 * mm + .18 * mm, "offsetDistance" : 25.4 * mm, "symmetric" : true});
        }
        {
            var Q0;
            {var subQ7=sQuery(id+"F0.wireOp",EDGE,"E0");var subQ9=sQuery(id+"F0.wireOp",EDGE,"E26.left");var subQ10=makeQuery(id+"F0.imprint","INTERSECT",VERTEX,{"derivedFrom":[subQ7,subQ9]});Q0=makeQuery(id+"F0.imprint","IMPRINT",FACE,{"disambiguationData":[TD([[makeQuery(id+"F0.imprint","IMPRINT",EDGE,{"disambiguationData":[TD([[subQ10,-1.0]])],"derivedFrom":subQ7}),1.0]])]});}
            var Q1;
            {var subQ5=sQuery(id+"F0.wireOp",EDGE,"E22.right");var subQ7=sQuery(id+"F0.wireOp",EDGE,"E0");var subQ8=makeQuery(id+"F0.imprint","INTERSECT",VERTEX,{"derivedFrom":[subQ7,subQ5]});Q1=makeQuery(id+"F0.imprint","IMPRINT",FACE,{"disambiguationData":[TD([[makeQuery(id+"F0.imprint","IMPRINT",EDGE,{"disambiguationData":[TD([[subQ8,-1.0]])],"derivedFrom":subQ7}),1.0]])]});}
            var Q2;
            {var subQ0=sQuery(id+"F0.wireOp",EDGE,"E24.right");var subQ3=sQuery(id+"F0.wireOp",EDGE,"E0");var subQ4=makeQuery(id+"F0.imprint","INTERSECT",VERTEX,{"derivedFrom":[subQ3,subQ0]});Q2=makeQuery(id+"F0.imprint","IMPRINT",FACE,{"disambiguationData":[TD([[makeQuery(id+"F0.imprint","IMPRINT",EDGE,{"disambiguationData":[TD([[subQ4,-1.0]])],"derivedFrom":subQ3}),1.0]])]});}
            var Q3;
            {var subQ0=sQuery(id+"F0.wireOp",EDGE,"E26.left");var subQ1=sQuery(id+"F0.wireOp",EDGE,"E0");var subQ2=makeQuery(id+"F0.imprint","INTERSECT",VERTEX,{"derivedFrom":[subQ1,subQ0]});Q3=makeQuery(id+"F0.imprint","IMPRINT",FACE,{"disambiguationData":[TD([[makeQuery(id+"F0.imprint","IMPRINT",EDGE,{"disambiguationData":[TD([[subQ2,-1.0]])],"derivedFrom":subQ1}),-1.0]])]});}
            var Q4;
            {var subQ0=sQuery(id+"F0.wireOp",EDGE,"E22.right");var subQ1=sQuery(id+"F0.wireOp",EDGE,"E0");var subQ2=makeQuery(id+"F0.imprint","INTERSECT",VERTEX,{"derivedFrom":[subQ1,subQ0]});Q4=makeQuery(id+"F0.imprint","IMPRINT",FACE,{"disambiguationData":[TD([[makeQuery(id+"F0.imprint","IMPRINT",EDGE,{"disambiguationData":[TD([[subQ2,-1.0]])],"derivedFrom":subQ1}),-1.0]])]});}
            var Q5;
            {var subQ0=sQuery(id+"F0.wireOp",EDGE,"E24.right");var subQ1=sQuery(id+"F0.wireOp",EDGE,"E0");var subQ2=makeQuery(id+"F0.imprint","INTERSECT",VERTEX,{"derivedFrom":[subQ1,subQ0]});Q5=makeQuery(id+"F0.imprint","IMPRINT",FACE,{"disambiguationData":[TD([[makeQuery(id+"F0.imprint","IMPRINT",EDGE,{"disambiguationData":[TD([[subQ2,-1.0]])],"derivedFrom":subQ1}),-1.0]])]});}
            extrude(context, id + "F11", {"entities" : qUnion([Q0, Q1, Q2, Q3, Q4, Q5]), "depth" : 1.2 * mm + .18 * mm, "offsetDistance" : 25.4 * mm, "symmetric" : true});
        }
        {
            var Q0;
            {var subQ7=sQuery(id+"F0.wireOp",EDGE,"E0");var subQ9=sQuery(id+"F0.wireOp",EDGE,"E28.left");var subQ10=makeQuery(id+"F0.imprint","INTERSECT",VERTEX,{"derivedFrom":[subQ7,subQ9]});Q0=makeQuery(id+"F0.imprint","IMPRINT",FACE,{"disambiguationData":[TD([[makeQuery(id+"F0.imprint","IMPRINT",EDGE,{"disambiguationData":[TD([[subQ10,-1.0]])],"derivedFrom":subQ7}),1.0]])]});}
            var Q1;
            {var subQ0=sQuery(id+"F0.wireOp",EDGE,"E24.right");var subQ3=sQuery(id+"F0.wireOp",EDGE,"E0");var subQ4=makeQuery(id+"F0.imprint","INTERSECT",VERTEX,{"derivedFrom":[subQ3,subQ0]});Q1=makeQuery(id+"F0.imprint","IMPRINT",FACE,{"disambiguationData":[TD([[makeQuery(id+"F0.imprint","IMPRINT",EDGE,{"disambiguationData":[TD([[subQ4,-1.0]])],"derivedFrom":subQ3}),1.0]])]});}
            var Q2;
            {var subQ0=sQuery(id+"F0.wireOp",EDGE,"E28.left");var subQ1=sQuery(id+"F0.wireOp",EDGE,"E0");var subQ2=makeQuery(id+"F0.imprint","INTERSECT",VERTEX,{"derivedFrom":[subQ1,subQ0]});Q2=makeQuery(id+"F0.imprint","IMPRINT",FACE,{"disambiguationData":[TD([[makeQuery(id+"F0.imprint","IMPRINT",EDGE,{"disambiguationData":[TD([[subQ2,-1.0]])],"derivedFrom":subQ1}),-1.0]])]});}
            var Q3;
            {var subQ0=sQuery(id+"F0.wireOp",EDGE,"E24.right");var subQ1=sQuery(id+"F0.wireOp",EDGE,"E0");var subQ2=makeQuery(id+"F0.imprint","INTERSECT",VERTEX,{"derivedFrom":[subQ1,subQ0]});Q3=makeQuery(id+"F0.imprint","IMPRINT",FACE,{"disambiguationData":[TD([[makeQuery(id+"F0.imprint","IMPRINT",EDGE,{"disambiguationData":[TD([[subQ2,-1.0]])],"derivedFrom":subQ1}),-1.0]])]});}
            var Q4;
            {var subQ0=sQuery(id+"F0.wireOp",EDGE,"E26.right");var subQ1=sQuery(id+"F0.wireOp",EDGE,"E0");var subQ2=makeQuery(id+"F0.imprint","INTERSECT",VERTEX,{"derivedFrom":[subQ1,subQ0]});Q4=makeQuery(id+"F0.imprint","IMPRINT",FACE,{"disambiguationData":[TD([[makeQuery(id+"F0.imprint","IMPRINT",EDGE,{"disambiguationData":[TD([[subQ2,-1.0]])],"derivedFrom":subQ1}),-1.0]])]});}
            var Q5;
            {var subQ0=sQuery(id+"F0.wireOp",EDGE,"E26.right");var subQ3=sQuery(id+"F0.wireOp",EDGE,"E0");var subQ4=makeQuery(id+"F0.imprint","INTERSECT",VERTEX,{"derivedFrom":[subQ3,subQ0]});Q5=makeQuery(id+"F0.imprint","IMPRINT",FACE,{"disambiguationData":[TD([[makeQuery(id+"F0.imprint","IMPRINT",EDGE,{"disambiguationData":[TD([[subQ4,-1.0]])],"derivedFrom":subQ3}),1.0]])]});}
            extrude(context, id + "F12", {"entities" : qUnion([Q0, Q1, Q2, Q3, Q4, Q5]), "depth" : 1.2 * mm + .18 * mm, "offsetDistance" : 25.4 * mm, "symmetric" : true});
        }
        {
            var Q0;
            {var subQ7=sQuery(id+"F0.wireOp",EDGE,"E0");var subQ9=sQuery(id+"F0.wireOp",EDGE,"E30.left");var subQ10=makeQuery(id+"F0.imprint","INTERSECT",VERTEX,{"derivedFrom":[subQ7,subQ9]});Q0=makeQuery(id+"F0.imprint","IMPRINT",FACE,{"disambiguationData":[TD([[makeQuery(id+"F0.imprint","IMPRINT",EDGE,{"disambiguationData":[TD([[subQ10,-1.0]])],"derivedFrom":subQ7}),1.0]])]});}
            var Q1;
            {var subQ0=sQuery(id+"F0.wireOp",EDGE,"E26.right");var subQ3=sQuery(id+"F0.wireOp",EDGE,"E0");var subQ4=makeQuery(id+"F0.imprint","INTERSECT",VERTEX,{"derivedFrom":[subQ3,subQ0]});Q1=makeQuery(id+"F0.imprint","IMPRINT",FACE,{"disambiguationData":[TD([[makeQuery(id+"F0.imprint","IMPRINT",EDGE,{"disambiguationData":[TD([[subQ4,-1.0]])],"derivedFrom":subQ3}),1.0]])]});}
            var Q2;
            {var subQ0=sQuery(id+"F0.wireOp",EDGE,"E30.left");var subQ1=sQuery(id+"F0.wireOp",EDGE,"E0");var subQ2=makeQuery(id+"F0.imprint","INTERSECT",VERTEX,{"derivedFrom":[subQ1,subQ0]});Q2=makeQuery(id+"F0.imprint","IMPRINT",FACE,{"disambiguationData":[TD([[makeQuery(id+"F0.imprint","IMPRINT",EDGE,{"disambiguationData":[TD([[subQ2,-1.0]])],"derivedFrom":subQ1}),-1.0]])]});}
            var Q3;
            {var subQ0=sQuery(id+"F0.wireOp",EDGE,"E26.right");var subQ1=sQuery(id+"F0.wireOp",EDGE,"E0");var subQ2=makeQuery(id+"F0.imprint","INTERSECT",VERTEX,{"derivedFrom":[subQ1,subQ0]});Q3=makeQuery(id+"F0.imprint","IMPRINT",FACE,{"disambiguationData":[TD([[makeQuery(id+"F0.imprint","IMPRINT",EDGE,{"disambiguationData":[TD([[subQ2,-1.0]])],"derivedFrom":subQ1}),-1.0]])]});}
            var Q4;
            {var subQ0=sQuery(id+"F0.wireOp",EDGE,"E28.right");var subQ3=sQuery(id+"F0.wireOp",EDGE,"E0");var subQ4=makeQuery(id+"F0.imprint","INTERSECT",VERTEX,{"derivedFrom":[subQ3,subQ0]});Q4=makeQuery(id+"F0.imprint","IMPRINT",FACE,{"disambiguationData":[TD([[makeQuery(id+"F0.imprint","IMPRINT",EDGE,{"disambiguationData":[TD([[subQ4,-1.0]])],"derivedFrom":subQ3}),1.0]])]});}
            var Q5;
            {var subQ0=sQuery(id+"F0.wireOp",EDGE,"E28.right");var subQ1=sQuery(id+"F0.wireOp",EDGE,"E0");var subQ2=makeQuery(id+"F0.imprint","INTERSECT",VERTEX,{"derivedFrom":[subQ1,subQ0]});Q5=makeQuery(id+"F0.imprint","IMPRINT",FACE,{"disambiguationData":[TD([[makeQuery(id+"F0.imprint","IMPRINT",EDGE,{"disambiguationData":[TD([[subQ2,-1.0]])],"derivedFrom":subQ1}),-1.0]])]});}
            extrude(context, id + "F13", {"entities" : qUnion([Q0, Q1, Q2, Q3, Q4, Q5]), "depth" : 1.2 * mm + .18 * mm, "offsetDistance" : 25.4 * mm, "symmetric" : true});
        }
        {
            var Q0;
            {var subQ0=sQuery(id+"F0.wireOp",EDGE,"E28.right");var subQ3=sQuery(id+"F0.wireOp",EDGE,"E0");var subQ4=makeQuery(id+"F0.imprint","INTERSECT",VERTEX,{"derivedFrom":[subQ3,subQ0]});Q0=makeQuery(id+"F0.imprint","IMPRINT",FACE,{"disambiguationData":[TD([[makeQuery(id+"F0.imprint","IMPRINT",EDGE,{"disambiguationData":[TD([[subQ4,-1.0]])],"derivedFrom":subQ3}),1.0]])]});}
            var Q1;
            {var subQ5=sQuery(id+"F0.wireOp",EDGE,"E2.left");var subQ9=sQuery(id+"F0.wireOp",EDGE,"E0");var subQ10=makeQuery(id+"F0.imprint","INTERSECT",VERTEX,{"derivedFrom":[subQ9,subQ5]});Q1=makeQuery(id+"F0.imprint","IMPRINT",FACE,{"disambiguationData":[TD([[makeQuery(id+"F0.imprint","IMPRINT",EDGE,{"disambiguationData":[TD([[subQ10,-1.0]])],"derivedFrom":subQ9}),1.0]])]});}
            var Q2;
            {var subQ0=sQuery(id+"F0.wireOp",EDGE,"E2.left");var subQ1=sQuery(id+"F0.wireOp",EDGE,"E0");var subQ2=makeQuery(id+"F0.imprint","INTERSECT",VERTEX,{"derivedFrom":[subQ1,subQ0]});Q2=makeQuery(id+"F0.imprint","IMPRINT",FACE,{"disambiguationData":[TD([[makeQuery(id+"F0.imprint","IMPRINT",EDGE,{"disambiguationData":[TD([[subQ2,-1.0]])],"derivedFrom":subQ1}),-1.0]])]});}
            var Q3;
            {var subQ3=sQuery(id+"F0.wireOp",EDGE,"E0");var subQ5=sQuery(id+"F0.wireOp",EDGE,"E35");var subQ9=makeQuery(id+"F0.imprint","INTERSECT",VERTEX,{"derivedFrom":[subQ3,subQ5]});Q3=makeQuery(id+"F0.imprint","IMPRINT",FACE,{"disambiguationData":[TD([[makeQuery(id+"F0.imprint","IMPRINT",EDGE,{"disambiguationData":[TD([[subQ9,-1.0]])],"derivedFrom":subQ3}),1.0]])]});}
            var Q4;
            {var subQ0=sQuery(id+"F0.wireOp",EDGE,"E28.right");var subQ1=sQuery(id+"F0.wireOp",EDGE,"E0");var subQ2=makeQuery(id+"F0.imprint","INTERSECT",VERTEX,{"derivedFrom":[subQ1,subQ0]});Q4=makeQuery(id+"F0.imprint","IMPRINT",FACE,{"disambiguationData":[TD([[makeQuery(id+"F0.imprint","IMPRINT",EDGE,{"disambiguationData":[TD([[subQ2,-1.0]])],"derivedFrom":subQ1}),-1.0]])]});}
            var Q5;
            {var subQ0=sQuery(id+"F0.wireOp",EDGE,"E35");var subQ1=sQuery(id+"F0.wireOp",EDGE,"E0");var subQ2=makeQuery(id+"F0.imprint","INTERSECT",VERTEX,{"derivedFrom":[subQ1,subQ0]});Q5=makeQuery(id+"F0.imprint","IMPRINT",FACE,{"disambiguationData":[TD([[makeQuery(id+"F0.imprint","IMPRINT",EDGE,{"disambiguationData":[TD([[subQ2,-1.0]])],"derivedFrom":subQ1}),-1.0]])]});}
            extrude(context, id + "F14", {"entities" : qUnion([Q0, Q1, Q2, Q3, Q4, Q5]), "depth" : 1.2 * mm + .18 * mm, "offsetDistance" : 25.4 * mm, "symmetric" : true});
        }
        {
            var Q0;
            {var subQ5=sQuery(id+"F0.wireOp",EDGE,"E2.right");var subQ7=sQuery(id+"F0.wireOp",EDGE,"E0");var subQ8=makeQuery(id+"F0.imprint","INTERSECT",VERTEX,{"derivedFrom":[subQ7,subQ5]});Q0=makeQuery(id+"F0.imprint","IMPRINT",FACE,{"disambiguationData":[TD([[makeQuery(id+"F0.imprint","IMPRINT",EDGE,{"disambiguationData":[TD([[subQ8,-1.0]])],"derivedFrom":subQ7}),1.0]])]});}
            var Q1;
            {var subQ0=sQuery(id+"F0.wireOp",EDGE,"E4.left");var subQ3=sQuery(id+"F0.wireOp",EDGE,"E0");var subQ4=makeQuery(id+"F0.imprint","INTERSECT",VERTEX,{"derivedFrom":[subQ3,subQ0]});Q1=makeQuery(id+"F0.imprint","IMPRINT",FACE,{"disambiguationData":[TD([[makeQuery(id+"F0.imprint","IMPRINT",EDGE,{"disambiguationData":[TD([[subQ4,-1.0]])],"derivedFrom":subQ3}),1.0]])]});}
            var Q2;
            {var subQ3=sQuery(id+"F0.wireOp",EDGE,"E0");var subQ5=sQuery(id+"F0.wireOp",EDGE,"E35");var subQ9=makeQuery(id+"F0.imprint","INTERSECT",VERTEX,{"derivedFrom":[subQ3,subQ5]});Q2=makeQuery(id+"F0.imprint","IMPRINT",FACE,{"disambiguationData":[TD([[makeQuery(id+"F0.imprint","IMPRINT",EDGE,{"disambiguationData":[TD([[subQ9,-1.0]])],"derivedFrom":subQ3}),1.0]])]});}
            var Q3;
            {var subQ0=sQuery(id+"F0.wireOp",EDGE,"E4.left");var subQ1=sQuery(id+"F0.wireOp",EDGE,"E0");var subQ2=makeQuery(id+"F0.imprint","INTERSECT",VERTEX,{"derivedFrom":[subQ1,subQ0]});Q3=makeQuery(id+"F0.imprint","IMPRINT",FACE,{"disambiguationData":[TD([[makeQuery(id+"F0.imprint","IMPRINT",EDGE,{"disambiguationData":[TD([[subQ2,-1.0]])],"derivedFrom":subQ1}),-1.0]])]});}
            var Q4;
            {var subQ0=sQuery(id+"F0.wireOp",EDGE,"E35");var subQ1=sQuery(id+"F0.wireOp",EDGE,"E0");var subQ2=makeQuery(id+"F0.imprint","INTERSECT",VERTEX,{"derivedFrom":[subQ1,subQ0]});Q4=makeQuery(id+"F0.imprint","IMPRINT",FACE,{"disambiguationData":[TD([[makeQuery(id+"F0.imprint","IMPRINT",EDGE,{"disambiguationData":[TD([[subQ2,-1.0]])],"derivedFrom":subQ1}),-1.0]])]});}
            var Q5;
            {var subQ0=sQuery(id+"F0.wireOp",EDGE,"E2.right");var subQ1=sQuery(id+"F0.wireOp",EDGE,"E0");var subQ2=makeQuery(id+"F0.imprint","INTERSECT",VERTEX,{"derivedFrom":[subQ1,subQ0]});Q5=makeQuery(id+"F0.imprint","IMPRINT",FACE,{"disambiguationData":[TD([[makeQuery(id+"F0.imprint","IMPRINT",EDGE,{"disambiguationData":[TD([[subQ2,-1.0]])],"derivedFrom":subQ1}),-1.0]])]});}
            extrude(context, id + "F15", {"entities" : qUnion([Q0, Q1, Q2, Q3, Q4, Q5]), "depth" : 1.2 * mm + .18 * mm, "offsetDistance" : 25.4 * mm, "symmetric" : true});
        }
        {
            var Q0;
            {var subQ7=sQuery(id+"F0.wireOp",EDGE,"E0");var subQ9=sQuery(id+"F0.wireOp",EDGE,"E6.left");var subQ10=makeQuery(id+"F0.imprint","INTERSECT",VERTEX,{"derivedFrom":[subQ7,subQ9]});Q0=makeQuery(id+"F0.imprint","IMPRINT",FACE,{"disambiguationData":[TD([[makeQuery(id+"F0.imprint","IMPRINT",EDGE,{"disambiguationData":[TD([[subQ10,-1.0]])],"derivedFrom":subQ7}),1.0]])]});}
            var Q1;
            {var subQ0=sQuery(id+"F0.wireOp",EDGE,"E4.right");var subQ3=sQuery(id+"F0.wireOp",EDGE,"E0");var subQ4=makeQuery(id+"F0.imprint","INTERSECT",VERTEX,{"derivedFrom":[subQ3,subQ0]});Q1=makeQuery(id+"F0.imprint","IMPRINT",FACE,{"disambiguationData":[TD([[makeQuery(id+"F0.imprint","IMPRINT",EDGE,{"disambiguationData":[TD([[subQ4,-1.0]])],"derivedFrom":subQ3}),1.0]])]});}
            var Q2;
            {var subQ5=sQuery(id+"F0.wireOp",EDGE,"E2.right");var subQ7=sQuery(id+"F0.wireOp",EDGE,"E0");var subQ8=makeQuery(id+"F0.imprint","INTERSECT",VERTEX,{"derivedFrom":[subQ7,subQ5]});Q2=makeQuery(id+"F0.imprint","IMPRINT",FACE,{"disambiguationData":[TD([[makeQuery(id+"F0.imprint","IMPRINT",EDGE,{"disambiguationData":[TD([[subQ8,-1.0]])],"derivedFrom":subQ7}),1.0]])]});}
            var Q3;
            {var subQ0=sQuery(id+"F0.wireOp",EDGE,"E6.left");var subQ1=sQuery(id+"F0.wireOp",EDGE,"E0");var subQ2=makeQuery(id+"F0.imprint","INTERSECT",VERTEX,{"derivedFrom":[subQ1,subQ0]});Q3=makeQuery(id+"F0.imprint","IMPRINT",FACE,{"disambiguationData":[TD([[makeQuery(id+"F0.imprint","IMPRINT",EDGE,{"disambiguationData":[TD([[subQ2,-1.0]])],"derivedFrom":subQ1}),-1.0]])]});}
            var Q4;
            {var subQ0=sQuery(id+"F0.wireOp",EDGE,"E2.right");var subQ1=sQuery(id+"F0.wireOp",EDGE,"E0");var subQ2=makeQuery(id+"F0.imprint","INTERSECT",VERTEX,{"derivedFrom":[subQ1,subQ0]});Q4=makeQuery(id+"F0.imprint","IMPRINT",FACE,{"disambiguationData":[TD([[makeQuery(id+"F0.imprint","IMPRINT",EDGE,{"disambiguationData":[TD([[subQ2,-1.0]])],"derivedFrom":subQ1}),-1.0]])]});}
            var Q5;
            {var subQ0=sQuery(id+"F0.wireOp",EDGE,"E4.right");var subQ1=sQuery(id+"F0.wireOp",EDGE,"E0");var subQ2=makeQuery(id+"F0.imprint","INTERSECT",VERTEX,{"derivedFrom":[subQ1,subQ0]});Q5=makeQuery(id+"F0.imprint","IMPRINT",FACE,{"disambiguationData":[TD([[makeQuery(id+"F0.imprint","IMPRINT",EDGE,{"disambiguationData":[TD([[subQ2,-1.0]])],"derivedFrom":subQ1}),-1.0]])]});}
            extrude(context, id + "F16", {"entities" : qUnion([Q0, Q1, Q2, Q3, Q4, Q5]), "depth" : 1.2 * mm + .18 * mm, "offsetDistance" : 25.4 * mm, "symmetric" : true});
        }
        {
            var Q0;
            Q0=makeQuery(id+"F1.opExtrude","CAP_FACE",FACE,{"disambiguationData":[OSD([sQuery(id+"F0.wireOp",EDGE,"E0"),sQuery(id+"F0.wireOp",EDGE,"E33")])],"isStart":false});
            var sketch = newSketch(context, id + "F17", { "sketchPlane" : qUnion([Q0])});
            skCircle(sketch, "E51", {"center": v(0, 0) * mm, "radius": 1.59 * mm});
            skSolve(sketch);
        }
        {
            var Q0;
            Q0=makeQuery(id+"F17.imprint","IMPRINT",FACE,{"disambiguationData":[TD([[makeQuery(id+"F17.imprint","IMPRINT",EDGE,{"derivedFrom":sQuery(id+"F17.wireOp",EDGE,"E51")}),1.0]])]});
            var Q1;
            Q1=makeQuery(id+"F17.imprint","IMPRINT",FACE,{"disambiguationData":[TD([[makeQuery(id+"F17.imprint","IMPRINT",EDGE,{"derivedFrom":sQuery(id+"F17.wireOp",EDGE,"E51")}),-1.0]])]});
            extrude(context, id + "F18", {"entities" : qUnion([Q0, Q1]), "oppositeDirection" : true, "depth" : 1.2 * mm, "offsetDistance" : 25.4 * mm, "hasSecondDirection" : true, "secondDirectionOppositeDirection" : false, "secondDirectionDepth" : 3.17 * mm});
        }
        {
            var Q0;
            Q0=makeQuery(id+"F17.imprint","IMPRINT",FACE,{"disambiguationData":[TD([[makeQuery(id+"F17.imprint","IMPRINT",EDGE,{"derivedFrom":sQuery(id+"F17.wireOp",EDGE,"E51")}),1.0]])]});
            extrude(context, id + "F19", {"entities" : qUnion([Q0]), "operationType" : NewBodyOperationType.REMOVE, "depth" : 3.17 * mm, "offsetDistance" : 25.4 * mm});
        }
        {
            var Q0;
            Q0=makeQuery(id+"F18.opExtrude","CAP_FACE",FACE,{"disambiguationData":[OSD([sQuery(id+"F0.wireOp",EDGE,"E33")])],"isStart":false});
            var sketch = newSketch(context, id + "F20", { "sketchPlane" : qUnion([Q0])});
            skCircle(sketch, "E52", {"center": v(0, 0) * mm, "radius": 12.7 * mm});
            skSolve(sketch);
        }
        {
            var Q0;
            Q0=makeQuery(id+"F20.imprint","IMPRINT",FACE,{"disambiguationData":[TD([[makeQuery(id+"F20.imprint","IMPRINT",EDGE,{"derivedFrom":sQuery(id+"F20.wireOp",EDGE,"E52")}),1.0]])]});
            var Q1;
            Q1=makeQuery(id+"F20.imprint","IMPRINT",FACE,{"disambiguationData":[TD([[makeQuery(id+"F20.imprint","IMPRINT",EDGE,{"derivedFrom":makeQuery(id+"F18.opExtrude","CAP_EDGE",EDGE,{"disambiguationData":[OSD([sQuery(id+"F0.wireOp",EDGE,"E33")])],"isStart":false})}),-1.0]])]});
            extrude(context, id + "F21", {"entities" : qUnion([Q0, Q1]), "operationType" : NewBodyOperationType.ADD, "depth" : 3.17 * mm, "offsetDistance" : 25.4 * mm});
        }
    });
